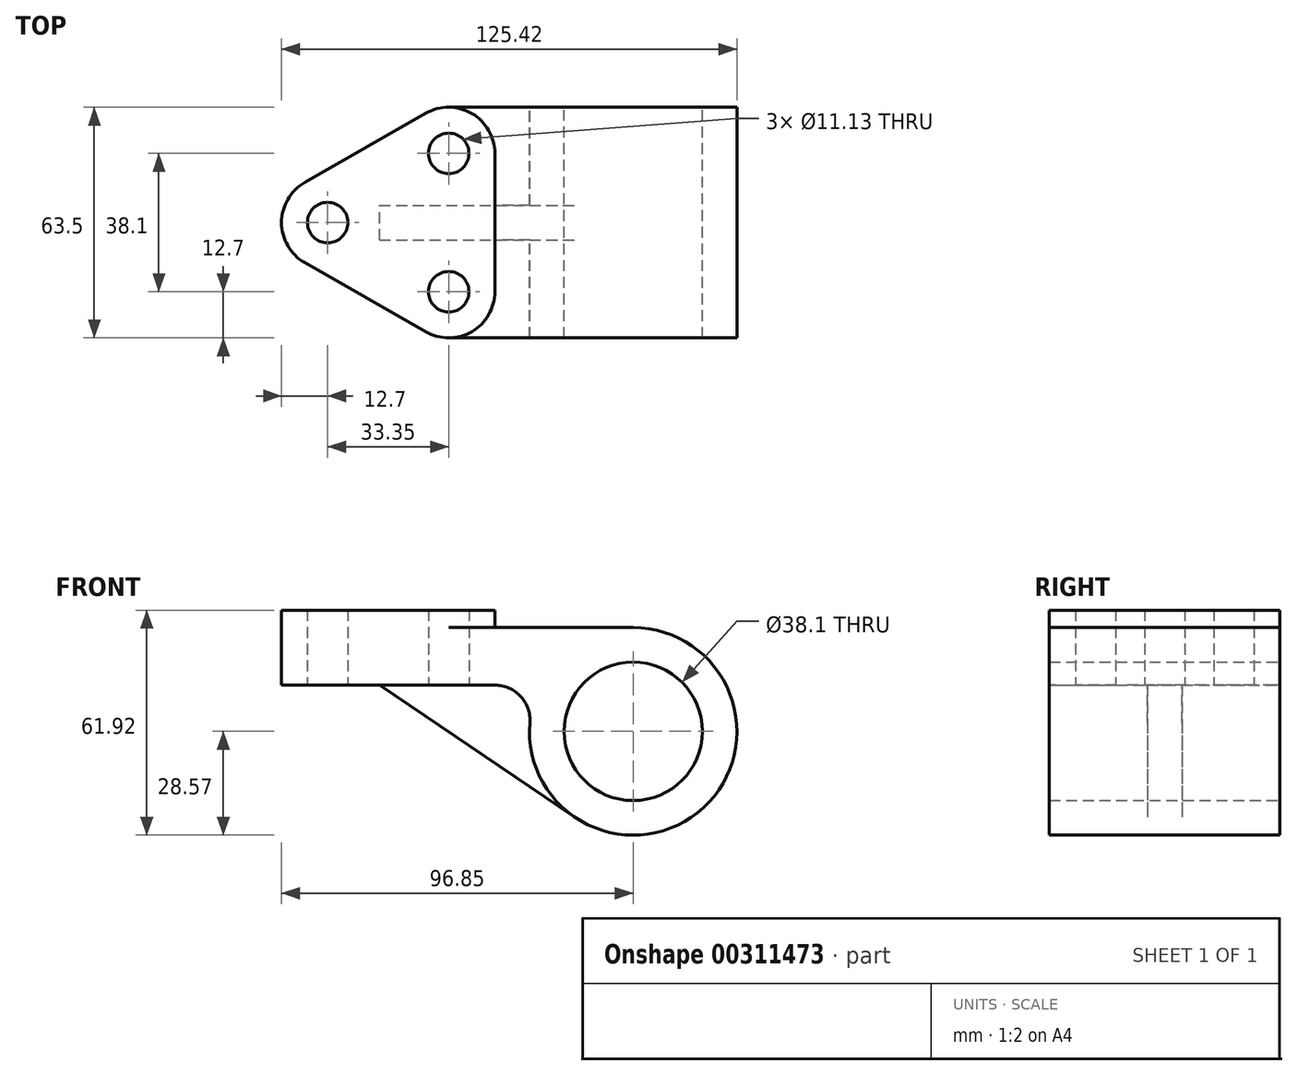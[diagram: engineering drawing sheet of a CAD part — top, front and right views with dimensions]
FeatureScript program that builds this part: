
annotation { "Feature Type Name" : "Feature", "Feature Type Description" : "" }
export const myFeature = defineFeature(function(context is Context, id is Id, definition is map)
    precondition{}
    {
        {
            var Q0;
            Q0=qCreatedBy(makeId("Front.planeOp"),FACE);
            var sketch = newSketch(context, id + "F0", { "sketchPlane" : qUnion([Q0])});
            skArc(sketch, "E0", {"start": v(-28.48, 2.38) * mm, "mid": v(19.35, -21.03) * mm, "end": v(0, 28.58) * mm});
            skLineSegment(sketch, "E1", {"start": v(0, 28.58) * mm, "end": v(-96.85, 28.57) * mm});
            skLineSegment(sketch, "E2", {"start": v(-96.85, 28.57) * mm, "end": v(-96.85, 12.7) * mm});
            skLineSegment(sketch, "E3", {"start": v(-96.85, 12.7) * mm, "end": v(-37.97, 12.7) * mm});
            skCircle(sketch, "E4", {"center": v(0, 0) * mm, "radius": 19.05 * mm});
            skArc(sketch, "E5", {"start": v(-28.48, 2.38) * mm, "mid": v(-30.96, 9.62) * mm, "end": v(-37.97, 12.7) * mm});
            skLineSegment(sketch, "E6", {"start": v(-69.85, 12.7) * mm, "end": v(-16, -23.68) * mm});
            skSolve(sketch);
        }
        {
            var Q0;
            {var subQ1=sQuery(id+"F0.wireOp",EDGE,"E1");Q0=makeQuery(id+"F0.imprint","IMPRINT",FACE,{"disambiguationData":[TD([[makeQuery(id+"F0.imprint","IMPRINT",EDGE,{"derivedFrom":subQ1}),1.0]])]});}
            extrude(context, id + "F1", {"entities" : qUnion([Q0]), "endBound" : BoundingType.SYMMETRIC, "depth" : 63.5 * mm});
        }
        {
            var Q0;
            {var subQ0=sQuery(id+"F0.wireOp",EDGE,"E5");Q0=makeQuery(id+"F0.imprint","IMPRINT",FACE,{"disambiguationData":[TD([[makeQuery(id+"F0.imprint","IMPRINT",EDGE,{"derivedFrom":subQ0}),1.0]])]});}
            extrude(context, id + "F2", {"entities" : qUnion([Q0]), "operationType" : NewBodyOperationType.ADD, "endBound" : BoundingType.SYMMETRIC, "depth" : 9.52 * mm});
        }
        {
            var Q0;
            Q0=makeQuery(id+"F1.opExtrude","SWEPT_FACE",FACE,{"disambiguationData":[OSD([sQuery(id+"F0.wireOp",EDGE,"E1")])]});
            var sketch = newSketch(context, id + "F3", { "sketchPlane" : qUnion([Q0])});
            skLineSegment(sketch, "E7", {"start": v(-90.45, -11.03) * mm, "end": v(-57.1, -30.08) * mm});
            skLineSegment(sketch, "E8", {"start": v(-90.45, 11.03) * mm, "end": v(-57.1, 30.08) * mm});
            skLineSegment(sketch, "E9", {"start": v(-38.1, -19.05) * mm, "end": v(-38.1, 19.05) * mm});
            skArc(sketch, "E10", {"start": v(-57.1, -30.08) * mm, "mid": v(-44.42, -30.03) * mm, "end": v(-38.1, -19.05) * mm});
            skArc(sketch, "E11", {"start": v(-38.1, 19.05) * mm, "mid": v(-44.42, 30.03) * mm, "end": v(-57.1, 30.08) * mm});
            skArc(sketch, "E12", {"start": v(-90.45, 11.03) * mm, "mid": v(-96.85, 0) * mm, "end": v(-90.45, -11.03) * mm});
            skLineSegment(sketch, "E13", {"start": v(0, 0) * mm, "end": v(-96.19, 0) * mm, "construction": true});
            skCircle(sketch, "E14", {"center": v(-84.15, 0) * mm, "radius": 5.56 * mm});
            skCircle(sketch, "E15", {"center": v(-50.8, -19.05) * mm, "radius": 5.56 * mm});
            skCircle(sketch, "E16", {"center": v(-50.8, 19.05) * mm, "radius": 5.56 * mm});
            skSolve(sketch);
        }
        {
            var Q0;
            {var subQ6=sQuery(id+"F3.wireOp",EDGE,"E7");Q0=makeQuery(id+"F3.imprint","IMPRINT",FACE,{"disambiguationData":[TD([[makeQuery(id+"F3.imprint","IMPRINT",EDGE,{"derivedFrom":subQ6}),-1.0]])]});}
            var Q1;
            {var subQ6=sQuery(id+"F3.wireOp",EDGE,"E8");Q1=makeQuery(id+"F3.imprint","IMPRINT",FACE,{"disambiguationData":[TD([[makeQuery(id+"F3.imprint","IMPRINT",EDGE,{"derivedFrom":subQ6}),1.0]])]});}
            extrude(context, id + "F4", {"entities" : qUnion([Q0, Q1]), "operationType" : NewBodyOperationType.REMOVE, "endBound" : BoundingType.UP_TO_NEXT, "oppositeDirection" : true, "depth" : 25.4 * mm});
        }
        {
            var Q0;
            {var subQ1=sQuery(id+"F3.wireOp",EDGE,"E7");Q0=makeQuery(id+"F3.imprint","IMPRINT",FACE,{"disambiguationData":[TD([[makeQuery(id+"F3.imprint","IMPRINT",EDGE,{"derivedFrom":subQ1}),1.0]])]});}
            extrude(context, id + "F5", {"entities" : qUnion([Q0]), "operationType" : NewBodyOperationType.ADD, "depth" : 4.78 * mm});
        }
        {
            var Q0;
            Q0=makeQuery(id+"F3.imprint","IMPRINT",FACE,{"disambiguationData":[TD([[makeQuery(id+"F3.imprint","IMPRINT",EDGE,{"derivedFrom":sQuery(id+"F3.wireOp",EDGE,"E15")}),1.0]])]});
            var Q1;
            Q1=makeQuery(id+"F3.imprint","IMPRINT",FACE,{"disambiguationData":[TD([[makeQuery(id+"F3.imprint","IMPRINT",EDGE,{"derivedFrom":sQuery(id+"F3.wireOp",EDGE,"E14")}),1.0]])]});
            var Q2;
            Q2=makeQuery(id+"F3.imprint","IMPRINT",FACE,{"disambiguationData":[TD([[makeQuery(id+"F3.imprint","IMPRINT",EDGE,{"derivedFrom":sQuery(id+"F3.wireOp",EDGE,"E16")}),1.0]])]});
            extrude(context, id + "F6", {"entities" : qUnion([Q0, Q1, Q2]), "operationType" : NewBodyOperationType.REMOVE, "endBound" : BoundingType.THROUGH_ALL, "oppositeDirection" : true, "depth" : 25.4 * mm});
        }
    });
